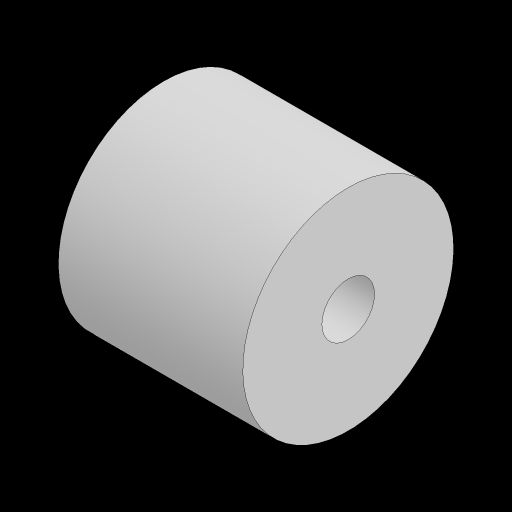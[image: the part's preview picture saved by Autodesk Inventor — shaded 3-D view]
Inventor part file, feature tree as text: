
AUTODESK INVENTOR PART (.ipt)
format: ipt  version: 2023.2 (Build 272271030, 271C)  size: 268,288 bytes
history: native  units: mm
features: revolve x1, sketch x1
ambient origin geometry x8: Origin, YZ Plane, XZ Plane, XY Plane, X Axis, Y Axis, Z Axis, Center Point
bodies: Solid1 (feature_tree)
feature tree (2):
  revolve  "Revolution1"  [1 undecoded]
  sketch  "Sketch1"  dims[d0=4.0mm d1=2.25mm d2=1.0mm d3=3.0mm d4=4.0mm d5=90.0deg]
note: 1 required parameter value undecoded (feature->parameter linkage not recoverable at this tier; creation-order binding heuristic only, values carry confidence <= 0.55)
